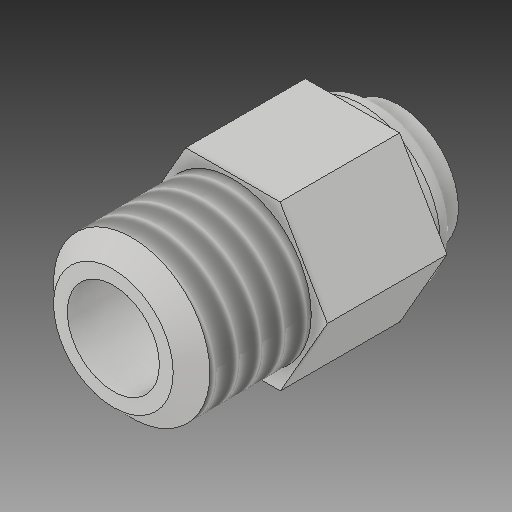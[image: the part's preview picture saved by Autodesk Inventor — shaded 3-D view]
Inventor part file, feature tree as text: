
AUTODESK INVENTOR PART (.ipt)
format: ipt  version: 2017 (Build 210142000, 142)  size: 175,616 bytes
history: native  units: mm
features: sketch x6, other x3
ambient origin geometry x8: Origin, YZ Plane, XZ Plane, XY Plane, X Axis, Y Axis, Z Axis, Center Point
bodies: Solid1 (feature_tree)
feature tree (9):
  other  "Pushfit-Adapter.ipt"
  other  "Solid1::Pushfit-Adapter.ipt"
  other  "TaggingFeature1"
  sketch  "Sketch1"  dims[d0=10.0mm]
  sketch  "Sketch2"
  sketch  "Sketch3"
  sketch  "Sketch4"
  sketch  "Sketch5"
  sketch  "Sketch6"
